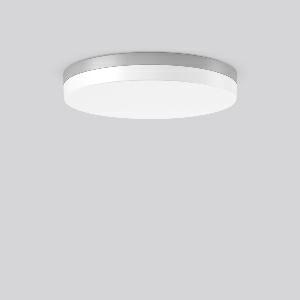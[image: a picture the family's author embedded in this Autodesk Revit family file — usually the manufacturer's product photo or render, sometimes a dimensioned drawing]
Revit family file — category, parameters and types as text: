
# Revit family: flat_slim_round_312633_004_730_9f50
name_source: partatom
category: Lighting Fixtures
units: mm (PartAtom-declared; Revit-internal decimal feet)

## family parameters
Cut with Voids When Loaded = No
Host = Face
Light Source = No
Part Type = Normal
Room Calculation Point = No
Round Connector Dimension = Use Diameter
Shared = No

## types (1)
- MultiLumen 1 830 (1 x LED Modul 830, 3350 lm, 3000)
    Apparent Load = 31 VA
    CIE Flux Codes = 41 71 90 86 100
    Color Rendering = 80
    Color Temperature = 3000
    Default Elevation = 1800 mm
    Height = 75 mm
    Lamp = 1 x LED Modul 830
    Lamp Light Flux = 3350 lm
    Lamp count = 1
    Length = 480 mm
    Lifetime = 50000 h
    Luminous efficacy = 108 lm/W
    Manufacturer = RZB
    ModVariant = No
    Model = 312633.004.730
    Mounting Place = Ceiling
    Mounting Type = Surface mounted
    Number of Poles = 1
    OnlyDefault = Yes
    Power Factor = 1
    Product Name = FLAT SLIM round
    Product group = Surface mounted ceiling and wall luminaires
    ProductGroupID = 305
    Protection Class = Protection class I
    Protection Degree = Degree of protection
    RLX_Detail_Level = 1
    RLX_Emergency_Light_Flux = 0 lm
    RLX_Emergency_Type = 0
    RLX_Emergency_Type_DB = No
    RlxData = <blob elided: 22001 chars, md5=f1914fb5>
    Socket = socket
    Standby Power = 0 W
    System Light Flux = 3350 lm
    System Power = 31 W
    Type Comments = MultiLumen 1 830
    Type Image = 312633.004.jpg
    URL = http://relux.com
    VarID = multilumen_1_830
    Voltage = 0 V
    Weight = 0.00 kg
    Width = 0 mm  [stored 0 ft]

note: [stored X ft] marks values corroborated as IEEE doubles in the binary element streams (Revit-internal decimal feet)

## geometry (parser evidence)
native form markers: Blend x4, Sweep x14
no freeform markers — native parametric forms only
